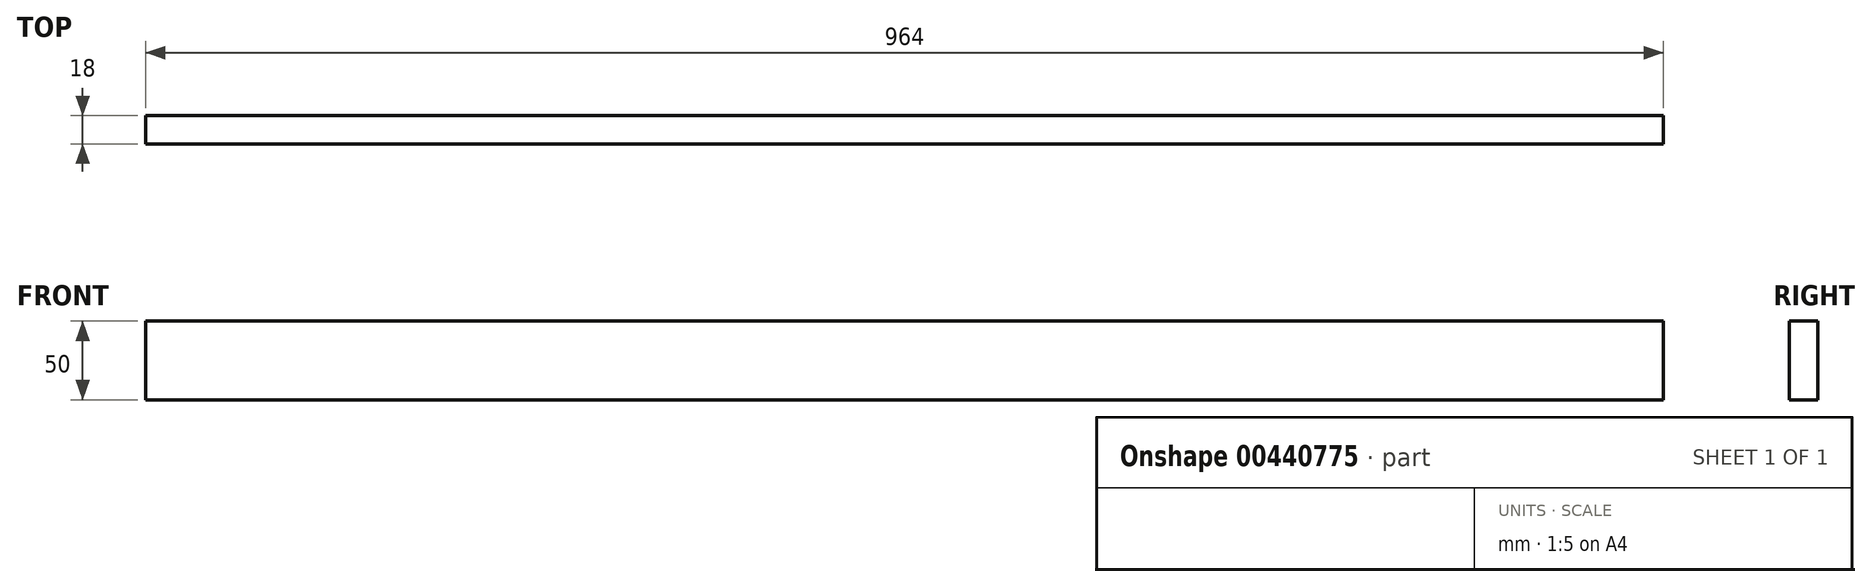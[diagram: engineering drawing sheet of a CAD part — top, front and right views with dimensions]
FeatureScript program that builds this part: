
annotation { "Feature Type Name" : "Feature", "Feature Type Description" : "" }
export const myFeature = defineFeature(function(context is Context, id is Id, definition is map)
    precondition{}
    {
        {
            var Q0;
            Q0=qCreatedBy(makeId("Front.planeOp"),FACE);
            var sketch = newSketch(context, id + "F0", { "sketchPlane" : qUnion([Q0])});
            skLineSegment(sketch, "E0.bottom", {"start": v(-964, 50) * mm, "end": v(0, 50) * mm});
            skLineSegment(sketch, "E0.top", {"start": v(-964, 0) * mm, "end": v(0, 0) * mm});
            skLineSegment(sketch, "E0.left", {"start": v(-964, 50) * mm, "end": v(-964, 0) * mm});
            skLineSegment(sketch, "E0.right", {"start": v(0, 50) * mm, "end": v(0, 0) * mm});
            skSolve(sketch);
        }
        {
            var Q0;
            Q0 = qSketchRegion(id + "F0", true);
            extrude(context, id + "F1", {"entities" : qUnion([Q0]), "depth" : 18 * mm});
        }
    });
